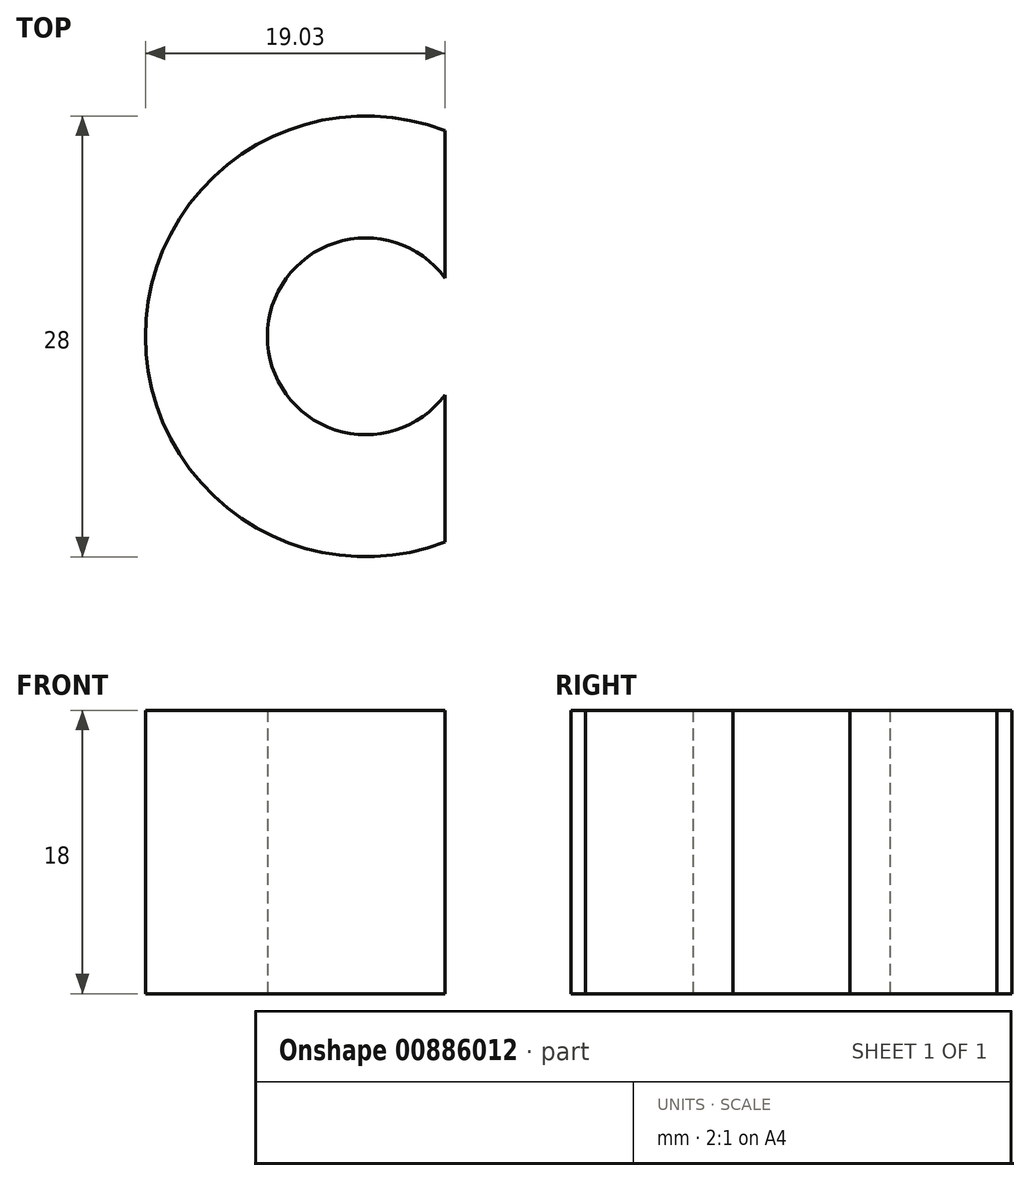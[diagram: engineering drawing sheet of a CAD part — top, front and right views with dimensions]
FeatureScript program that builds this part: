
annotation { "Feature Type Name" : "Feature", "Feature Type Description" : "" }
export const myFeature = defineFeature(function(context is Context, id is Id, definition is map)
    precondition{}
    {
        {
            var Q0;
            Q0=qCreatedBy(makeId("Top.planeOp"),FACE);
            var sketch = newSketch(context, id + "F0", { "sketchPlane" : qUnion([Q0])});
            skCircle(sketch, "E0", {"center": v(0, 0) * mm, "radius": 6.25 * mm});
            skCircle(sketch, "E1", {"center": v(0, 0) * mm, "radius": 14 * mm});
            skLineSegment(sketch, "E2", {"start": v(0, 0) * mm, "end": v(18.12, 0) * mm});
            skCircle(sketch, "E3", {"center": v(18.12, 0) * mm, "radius": 12.04 * mm});
            skLineSegment(sketch, "E4", {"start": v(6.25, 0) * mm, "end": v(6.25, -12.53) * mm});
            skLineSegment(sketch, "E5", {"start": v(6.25, -12.53) * mm, "end": v(6.25, 0) * mm});
            skLineSegment(sketch, "E6", {"start": v(6.25, 12.53) * mm, "end": v(6.25, 0) * mm});
            skLineSegment(sketch, "E7", {"start": v(5.03, -13.07) * mm, "end": v(5.03, 13.07) * mm});
            skSolve(sketch);
        }
        {
            var Q0;
            {var subQ0=sQuery(id+"F0.wireOp",EDGE,"E7");var subQ1=sQuery(id+"F0.wireOp",EDGE,"E0");var subQ2=makeQuery(id+"F0.imprint","INTERSECT",VERTEX,{"disambiguationData":[OD(0.0)],"derivedFrom":[subQ1,subQ0]});Q0=makeQuery(id+"F0.imprint","IMPRINT",FACE,{"disambiguationData":[TD([[makeQuery(id+"F0.imprint","IMPRINT",EDGE,{"disambiguationData":[TD([[subQ2,-1.0]])],"derivedFrom":subQ1}),-1.0]])]});}
            extrude(context, id + "F1", {"entities" : qUnion([Q0]), "depth" : 18 * mm, "offsetDistance" : 25 * mm});
        }
    });
